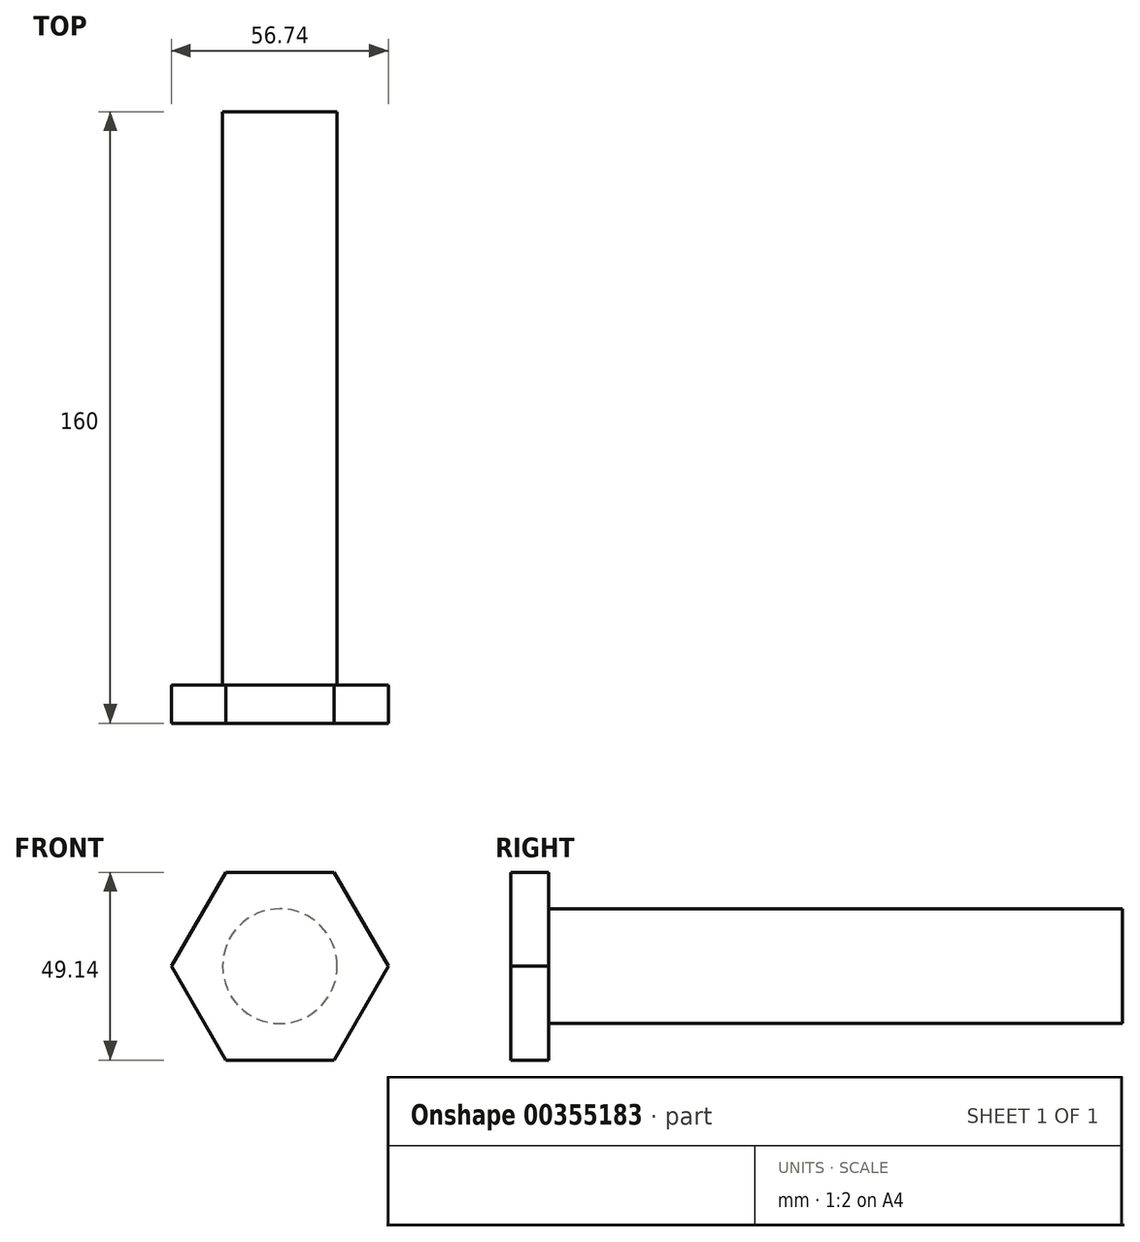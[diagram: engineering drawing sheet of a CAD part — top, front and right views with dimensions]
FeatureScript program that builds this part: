
annotation { "Feature Type Name" : "Feature", "Feature Type Description" : "" }
export const myFeature = defineFeature(function(context is Context, id is Id, definition is map)
    precondition{}
    {
        {
            var Q0;
            Q0=qCreatedBy(makeId("Front.planeOp"),FACE);
            var sketch = newSketch(context, id + "F0", { "sketchPlane" : qUnion([Q0])});
            skCircle(sketch, "E0", {"center": v(0, 0) * mm, "radius": 15 * mm});
            skSolve(sketch);
        }
        {
            var Q0;
            Q0=makeQuery(id+"F0.imprint","IMPRINT",FACE,{"disambiguationData":[TD([[makeQuery(id+"F0.imprint","IMPRINT",EDGE,{"derivedFrom":sQuery(id+"F0.wireOp",EDGE,"E0")}),1.0]])]});
            extrude(context, id + "F1", {"entities" : qUnion([Q0]), "endBound" : BoundingType.SYMMETRIC, "depth" : 150 * mm});
        }
        {
            var Q0;
            Q0=makeQuery(id+"F1.opExtrude","CAP_FACE",FACE,{"disambiguationData":[OSD([sQuery(id+"F0.wireOp",EDGE,"E0")])],"isStart":false});
            var sketch = newSketch(context, id + "F2", { "sketchPlane" : qUnion([Q0])});
            skCircle(sketch, "E1.cCircle", {"center": v(0, 0) * mm, "radius": 24.57 * mm, "construction": true});
            skLineSegment(sketch, "E1.0", {"start": v(14.18, 24.57) * mm, "end": v(28.37, 0) * mm});
            skLineSegment(sketch, "E1.1", {"start": v(28.37, 0) * mm, "end": v(14.18, -24.57) * mm});
            skLineSegment(sketch, "E1.2", {"start": v(14.18, -24.57) * mm, "end": v(-14.18, -24.57) * mm});
            skLineSegment(sketch, "E1.3", {"start": v(-14.18, -24.57) * mm, "end": v(-28.37, 0) * mm});
            skLineSegment(sketch, "E1.4", {"start": v(-28.37, 0) * mm, "end": v(-14.18, 24.57) * mm});
            skLineSegment(sketch, "E1.5", {"start": v(-14.18, 24.57) * mm, "end": v(14.18, 24.57) * mm});
            skPoint(sketch, "E1.0.midPoint", {"position": v(21.28, 12.28) * mm});
            skSolve(sketch);
        }
        {
            var Q0;
            Q0 = qSketchRegion(id + "F2", true);
            extrude(context, id + "F3", {"entities" : qUnion([Q0]), "operationType" : NewBodyOperationType.ADD, "depth" : 10 * mm});
        }
    });
